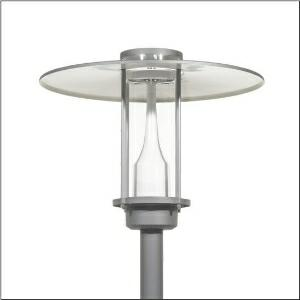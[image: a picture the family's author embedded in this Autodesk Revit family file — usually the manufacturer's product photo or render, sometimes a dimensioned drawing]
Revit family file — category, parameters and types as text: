
# Revit family: city-light_plus_iq___p1_0a_5xa5275lf14hp_bc32
name_source: partatom
category: Lighting Fixtures
units: mm (PartAtom-declared; Revit-internal decimal feet)

## family parameters
Cut with Voids When Loaded = No
Host = Face
Light Source = No
Part Type = Normal
Room Calculation Point = No
Round Connector Dimension = Use Diameter
Shared = No

## types (1)
- --- (1 x LED, 4680 lm, 33.6 W, 4000K)
    Apparent Load = 34 VA
    CIE Flux Codes = 30 60 90 96 100
    Color Rendering = 70
    Color Temperature = 4000K
    Default Elevation = 1800 mm
    Description = City-Light Plus iQ, mast luminaire, Module 540 iQ-SR, primary light control with 3 zone facetted reflector, of plastic, silver coated, highly specular, structured, primary optical cover: cover, of PMMA, transparent, light distribution: P1.0a, light emission: direct distribution, primary light characteristic: strongly asymmetric, installation type: post-top, LED, High Power LED, rated luminous flux: 4.680lm, luminous efficacy: 139lm/W, light colour: 740, colour temperature: 4000K, control gear: iQ Street-Remote, control: pre-setting: logarithmic dimming characteristic, Street-Remote, Auto-Match, Temp-Guard, Lumen-Switch, Night-Set, Smart-Wire, Light-Fading, Desk-Remote (wireless, voltage-free reading and setting of iQ features in the workshop via application-optimized NFC function/RFID function), optimised constant luminous flux control (CLO 2.0), with terminal, 6-pole, max. 2.5mm², mains connection: 230..240V, AC, 50/60Hz, start of lifetime: 34W, end of service life: 36W, reduction: 15W, luminaire housing, upper part, of glass-fibre reinforced polyester, coated, Siteco® metallic grey (DB 702S), diameter: 750mm, height: 590mm, spigot size: d x l = 76 x 70mm (post-top) | with reducer (optional accessory) 60 x 70mm, mounting height: 3..5m, post-top mast mounting element, of diecast aluminium, coated, Siteco® metallic grey (DB 702S), Module 540 iQ-SR, traffic white (RAL 9016), equipment: Power, protection rating (complete): IP65, insulation class (complete): insulation class II (safety insulation), certification: CE, ENEC, VDE, packaging unit: 1 piece

Light Distribution: P1.0a
    Height = 590 mm
    Lamp = 1 x LED
    Lamp Light Flux = 4680 lm
    Lamp Power = 33.6 W
    Lamp count = 1
    Length = 750 mm
    Luminous efficacy = 139 lm/W
    Manufacturer = Siteco
    ModVariant = No
    Model = 5XA5275LF14HP
    Number of Poles = 1
    OnlyDefault = Yes
    Power Factor = 1
    Product Name = City-Light Plus iQ | P1.0a
    Product group = mast luminaire | pylon top
    ProductGroupID = 6100
    Protection Class = Protection class II
    Protection Degree = IP 65
    RLX_Detail_Level = 1
    RLX_Emergency_Light_Flux = 0 lm
    RLX_Emergency_Type = 0
    RLX_Emergency_Type_DB = No
    RlxData = <blob elided: 35029 chars, md5=f19d67ed>
    Socket = socket
    Standby Power = 0 W
    System Light Flux = 4680 lm
    System Power = 34 W
    Type Comments = factory setting: luminous flux: 100 % | dim-lin: 254 | 695 mA
    Type Image = l_1006456.jpg
    URL = http://relux.com
    VarID = @adj_193696
    Voltage = 0 V
    Weight = 0.00 kg
    Width = 0 mm  [stored 0 ft]

note: [stored X ft] marks values corroborated as IEEE doubles in the binary element streams (Revit-internal decimal feet)

## geometry (parser evidence)
native form markers: Blend x4, Sweep x9
no freeform markers — native parametric forms only
